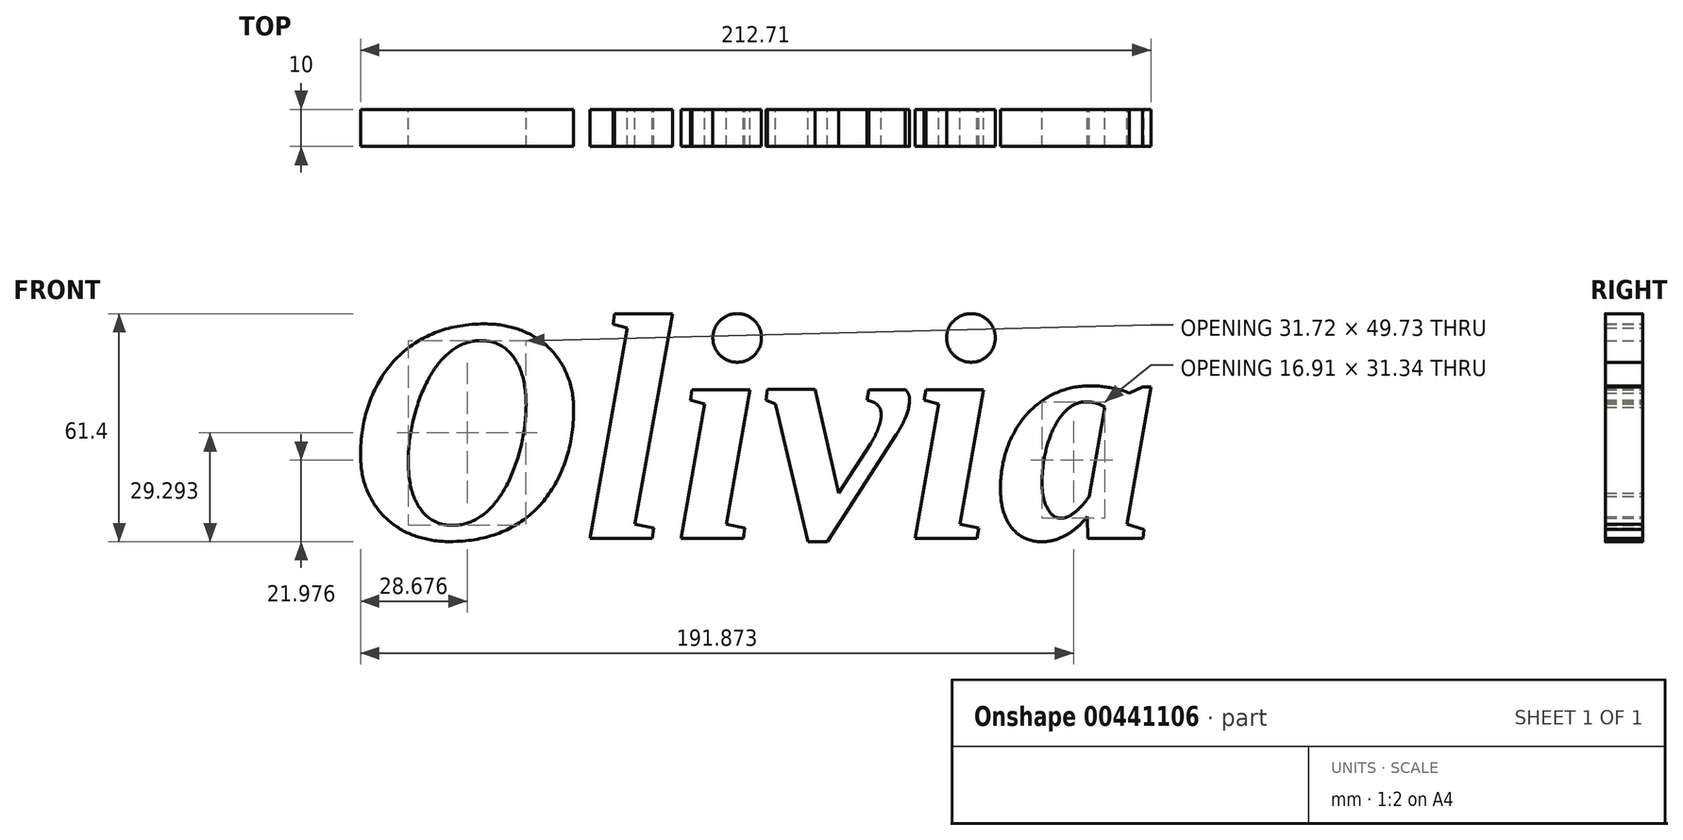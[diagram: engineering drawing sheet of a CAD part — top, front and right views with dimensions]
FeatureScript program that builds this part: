
annotation { "Feature Type Name" : "Feature", "Feature Type Description" : "" }
export const myFeature = defineFeature(function(context is Context, id is Id, definition is map)
    precondition{}
    {
        {
            var Q0;
            Q0=qCreatedBy(makeId("Front.planeOp"),FACE);
            var sketch = newSketch(context, id + "F0", { "sketchPlane" : qUnion([Q0])});
            skText(sketch, "E0", { "text": "Olivia", "fontName": "Tinos-BoldItalic.ttf"});
            const initialGuessF0  = {"E0": [-0.11023, -0.03375, 1, 0, 0.06278]};
            skSetInitialGuess(sketch, initialGuessF0);
            skSolve(sketch);
        }
        {
            var Q0;
            Q0 = qSketchRegion(id + "F0", true);
            extrude(context, id + "F1", {"entities" : qUnion([Q0]), "depth" : 10 * mm});
        }
    });
